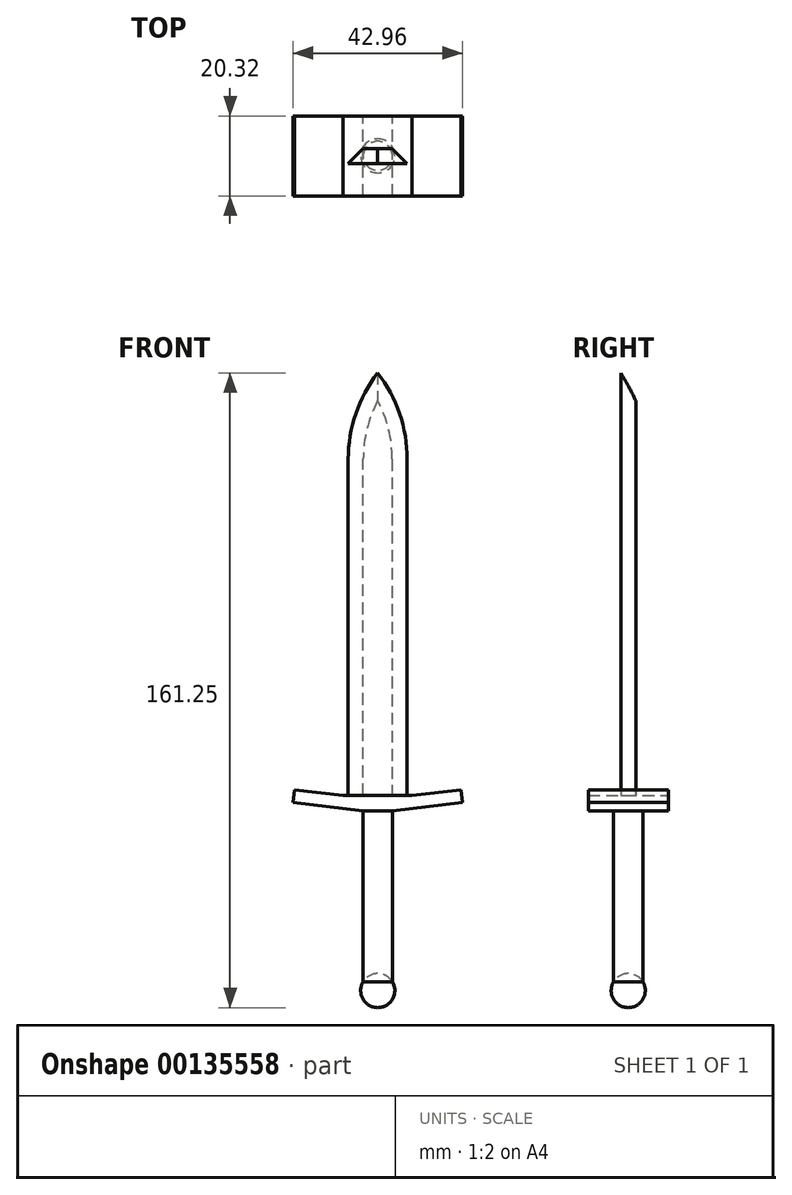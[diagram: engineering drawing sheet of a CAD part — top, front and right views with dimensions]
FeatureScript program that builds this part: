
annotation { "Feature Type Name" : "Feature", "Feature Type Description" : "" }
export const myFeature = defineFeature(function(context is Context, id is Id, definition is map)
    precondition{}
    {
        {
            var Q0;
            Q0=qCreatedBy(makeId("Front.planeOp"),FACE);
            var sketch = newSketch(context, id + "F0", { "sketchPlane" : qUnion([Q0])});
            skLineSegment(sketch, "E0", {"start": v(-8.76, -29.53) * mm, "end": v(-8.76, 55.85) * mm});
            skArc(sketch, "E1", {"start": v(0, 79.8) * mm, "mid": v(-6.5, 68.6) * mm, "end": v(-8.76, 55.85) * mm});
            skLineSegment(sketch, "E2.MirrorCS", {"start": v(8.76, -29.53) * mm, "end": v(8.76, 55.85) * mm});
            skArc(sketch, "E3.MirrorCS", {"start": v(0, 79.8) * mm, "mid": v(6.5, 68.6) * mm, "end": v(8.76, 55.85) * mm});
            skLineSegment(sketch, "E4.bottom", {"start": v(0, -33.54) * mm, "end": v(3.72, -33.54) * mm});
            skLineSegment(sketch, "E4.right", {"start": v(3.72, -33.54) * mm, "end": v(3.72, -79.15) * mm});
            skArc(sketch, "E5", {"start": v(0, -83.48) * mm, "mid": v(4.34, -79.15) * mm, "end": v(0, -74.8) * mm});
            skLineSegment(sketch, "E6", {"start": v(0, -33.54) * mm, "end": v(0, -83.48) * mm});
            skLineSegment(sketch, "E7", {"start": v(3.72, -33.54) * mm, "end": v(21.48, -31.36) * mm});
            skLineSegment(sketch, "E8", {"start": v(21.48, -31.36) * mm, "end": v(21.09, -28.21) * mm});
            skLineSegment(sketch, "E9", {"start": v(21.09, -28.21) * mm, "end": v(8.76, -29.53) * mm});
            skLineSegment(sketch, "E10.MirrorCS", {"start": v(-3.72, -33.54) * mm, "end": v(-21.48, -31.36) * mm});
            skLineSegment(sketch, "E11.MirrorCS", {"start": v(-21.09, -28.21) * mm, "end": v(-8.76, -29.53) * mm});
            skLineSegment(sketch, "E12.MirrorCS", {"start": v(-21.48, -31.36) * mm, "end": v(-21.09, -28.21) * mm});
            skLineSegment(sketch, "E13", {"start": v(-3.72, -33.54) * mm, "end": v(3.72, -33.54) * mm});
            skLineSegment(sketch, "E14", {"start": v(8.76, -29.53) * mm, "end": v(-8.76, -29.53) * mm});
            skSolve(sketch);
        }
        {
            var Q0;
            {var subQ2=sQuery(id+"F0.wireOp",EDGE,"E7");Q0=makeQuery(id+"F0.imprint","IMPRINT",FACE,{"disambiguationData":[TD([[makeQuery(id+"F0.imprint","IMPRINT",EDGE,{"derivedFrom":subQ2}),1.0]])]});}
            extrude(context, id + "F1", {"entities" : qUnion([Q0]), "endBound" : BoundingType.SYMMETRIC, "depth" : 20.32 * mm});
        }
        {
            var Q0;
            {var subQ4=sQuery(id+"F0.wireOp",EDGE,"E0");Q0=makeQuery(id+"F0.imprint","IMPRINT",FACE,{"disambiguationData":[TD([[makeQuery(id+"F0.imprint","IMPRINT",EDGE,{"derivedFrom":subQ4}),-1.0]])]});}
            var Q1;
            {var subQ4=sQuery(id+"F0.wireOp",EDGE,"E2.MirrorCS");Q1=makeQuery(id+"F0.imprint","IMPRINT",FACE,{"disambiguationData":[TD([[makeQuery(id+"F0.imprint","IMPRINT",EDGE,{"derivedFrom":subQ4}),1.0]])]});}
            extrude(context, id + "F2", {"entities" : qUnion([Q0, Q1]), "endBound" : BoundingType.SYMMETRIC, "depth" : 3.8 * mm});
        }
        {
            var Q0;
            {var subQ0=sQuery(id+"F0.wireOp",EDGE,"E4.bottom");Q0=makeQuery(id+"F0.imprint","IMPRINT",FACE,{"disambiguationData":[TD([[makeQuery(id+"F0.imprint","IMPRINT",EDGE,{"derivedFrom":subQ0}),-1.0]])]});}
            var Q1;
            {var subQ0=sQuery(id+"F0.wireOp",EDGE,"E6");var subQ1=sQuery(id+"F0.wireOp",EDGE,"E5");var subQ2=makeQuery(id+"F0.imprint","INTERSECT",VERTEX,{"disambiguationData":[OD(0.0)],"derivedFrom":[subQ1,subQ0]});Q1=makeQuery(id+"F0.imprint","IMPRINT",FACE,{"disambiguationData":[TD([[makeQuery(id+"F0.imprint","IMPRINT",EDGE,{"disambiguationData":[TD([[subQ2,-1.0]])],"derivedFrom":subQ1}),1.0]])]});}
            var Q2;
            Q2=sQuery(id+"F0.wireOp",EDGE,"E6");
            revolve(context, id + "F3", {"entities" : qUnion([Q0, Q1]), "axis" : qUnion([Q2]), "revolveType" : RevolveType.FULL});
        }
        {
            var Q0;
            Q0=makeQuery(id+"F2.opExtrude","CAP_EDGE",EDGE,{"disambiguationData":[OSD([sQuery(id+"F0.wireOp",EDGE,"E1")])],"isStart":true});
            var Q1;
            Q1=makeQuery(id+"F2.opExtrude","CAP_EDGE",EDGE,{"disambiguationData":[OSD([sQuery(id+"F0.wireOp",EDGE,"E3.MirrorCS")])],"isStart":true});
            chamfer(context, id + "F4", {"entities" : qUnion([Q0, Q1]), "width" : 5.08 * mm, "tangentPropagation" : true});
        }
        {
            var Q0;
            {var subQ3=sQuery(id+"F0.wireOp",EDGE,"E5");var subQ5=sQuery(id+"F0.wireOp",EDGE,"E6");var subQ6=makeQuery(id+"F0.imprint","INTERSECT",VERTEX,{"disambiguationData":[OD(1.0)],"derivedFrom":[subQ3,subQ5]});Q0=makeQuery(id+"F0.imprint","IMPRINT",FACE,{"disambiguationData":[TD([[makeQuery(id+"F0.imprint","IMPRINT",EDGE,{"disambiguationData":[TD([[subQ6,1.0]])],"derivedFrom":subQ3}),-1.0]])]});}
            var Q1;
            Q1=sQuery(id+"F0.wireOp",EDGE,"E6");
            revolve(context, id + "F5", {"entities" : qUnion([Q0]), "axis" : qUnion([Q1]), "revolveType" : RevolveType.FULL});
        }
    });
